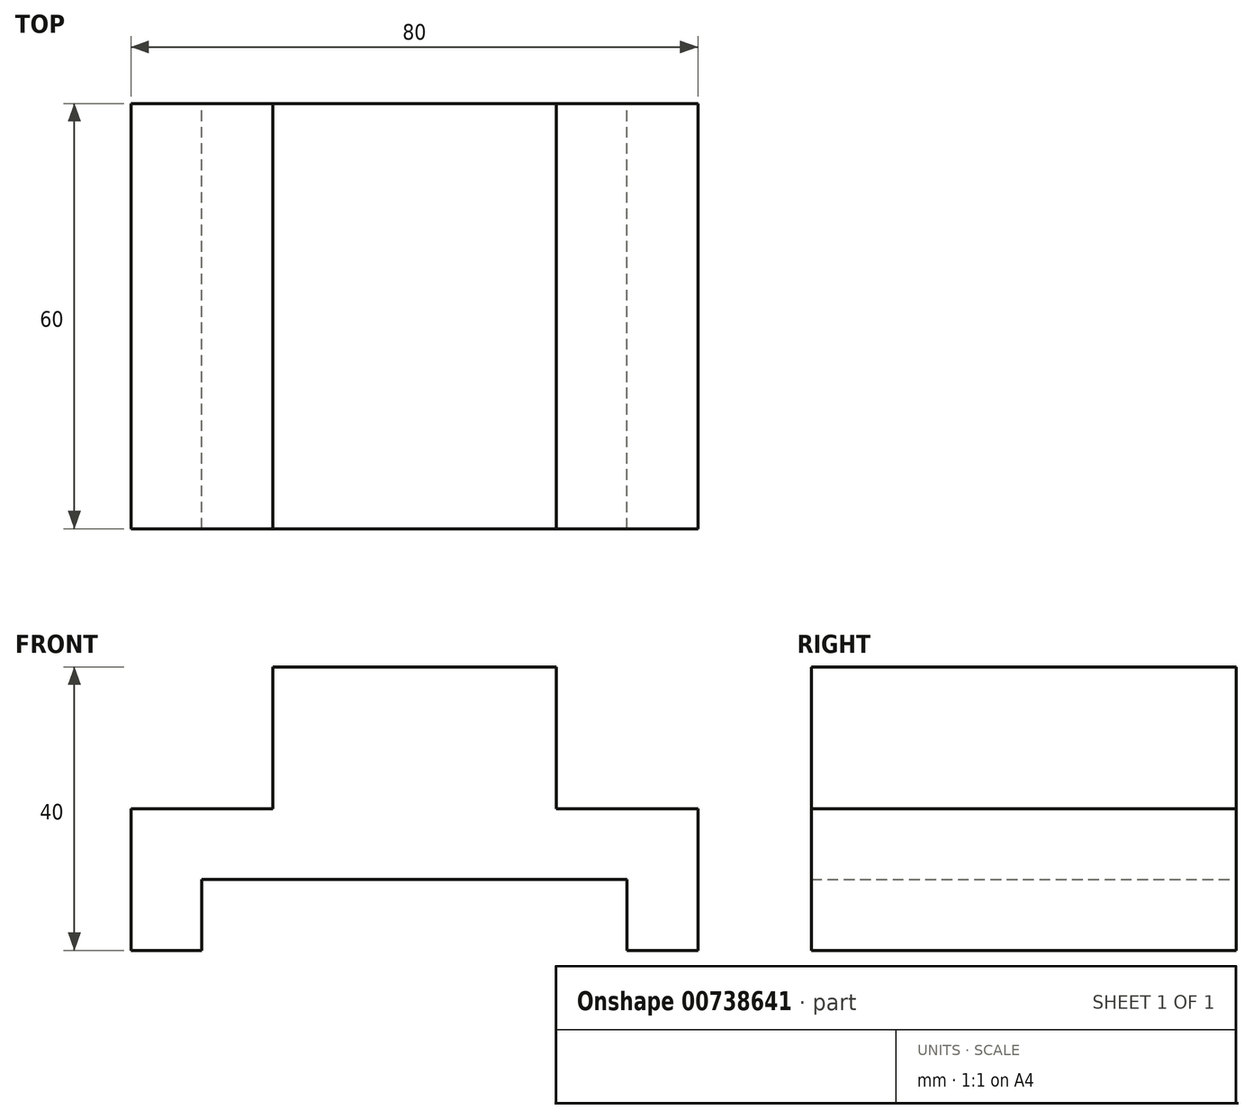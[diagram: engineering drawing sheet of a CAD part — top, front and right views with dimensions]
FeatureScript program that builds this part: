
annotation { "Feature Type Name" : "Feature", "Feature Type Description" : "" }
export const myFeature = defineFeature(function(context is Context, id is Id, definition is map)
    precondition{}
    {
        {
            var Q0;
            Q0=qCreatedBy(makeId("Front.planeOp"),FACE);
            var sketch = newSketch(context, id + "F0", { "sketchPlane" : qUnion([Q0])});
            skLineSegment(sketch, "E0", {"start": v(-40, -10) * mm, "end": v(-30, -10) * mm});
            skLineSegment(sketch, "E1", {"start": v(-30, -10) * mm, "end": v(-30, 0) * mm});
            skLineSegment(sketch, "E2", {"start": v(-30, 0) * mm, "end": v(0, 0) * mm});
            skLineSegment(sketch, "E3", {"start": v(0, 0) * mm, "end": v(0, 30) * mm, "construction": true});
            skLineSegment(sketch, "E4", {"start": v(0, 30) * mm, "end": v(-20, 30) * mm});
            skLineSegment(sketch, "E5", {"start": v(-20, 30) * mm, "end": v(-20, 10) * mm});
            skLineSegment(sketch, "E6", {"start": v(-20, 10) * mm, "end": v(-40, 10) * mm});
            skLineSegment(sketch, "E7", {"start": v(-40, 10) * mm, "end": v(-40, -10) * mm});
            skLineSegment(sketch, "E8.MirrorCS", {"start": v(40, -10) * mm, "end": v(30, -10) * mm});
            skLineSegment(sketch, "E9.MirrorCS", {"start": v(30, -10) * mm, "end": v(30, 0) * mm});
            skLineSegment(sketch, "E10.MirrorCS", {"start": v(20, 30) * mm, "end": v(20, 10) * mm});
            skLineSegment(sketch, "E11.MirrorCS", {"start": v(0, 30) * mm, "end": v(20, 30) * mm});
            skLineSegment(sketch, "E12.MirrorCS", {"start": v(20, 10) * mm, "end": v(40, 10) * mm});
            skLineSegment(sketch, "E13.MirrorCS", {"start": v(30, 0) * mm, "end": v(0, 0) * mm});
            skLineSegment(sketch, "E14.MirrorCS", {"start": v(40, 10) * mm, "end": v(40, -10) * mm});
            skSolve(sketch);
        }
        {
            var Q0;
            Q0 = qSketchRegion(id + "F0", true);
            extrude(context, id + "F1", {"entities" : qUnion([Q0]), "depth" : 60 * mm, "offsetDistance" : 25 * mm});
        }
    });
